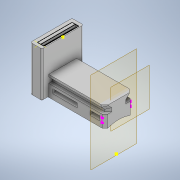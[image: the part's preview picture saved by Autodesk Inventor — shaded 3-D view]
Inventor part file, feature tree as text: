
AUTODESK INVENTOR PART (.ipt)
format: ipt  version: 2021.1 (Build 251245010, 245A)  size: 247,296 bytes
history: native  units: mm
features: move_body x5, extrude x4, sketch x4, direct_edit x2, plane x2, other x1
ambient origin geometry x8: Origin, YZ Plane, XZ Plane, XY Plane, X Axis, Y Axis, Z Axis, Center Point
bodies: Volumenkörper1 (feature_tree)
feature tree (18):
  direct_edit  "Direktbearbeitung1"
  extrude  "Extrusion1"  Depth=5.0mm TaperAngle=0.0deg
  plane  "Arbeitsebene4"
  sketch  "Skizze3"  dims[d6=0.0mm d7=0.0mm d8=-5.0mm d9=0.0mm d10=0.0mm d11=-6.75mm]
  plane  "Arbeitsebene3"
  extrude  "Extrusion2"  TaperAngle=0.0deg  [1 undecoded]
  sketch  "Skizze6"  dims[d18=10.0mm d19=0.0mm d20=2.0mm d21=0.0mm d22=1.9mm d23=0.0mm d24=0.0mm]
  extrude  "Extrusion3"  Depth=5.5mm TaperAngle=0.0deg
  extrude  "Extrusion4"  Depth=2.0mm TaperAngle=0.0deg
  direct_edit  "Direktbearbeitung2"
  sketch  "Skizze1"  dims[d0=0.0mm d1=0.0mm d2=15.75mm d3=5.0mm d4=0.0mm d5=0.0mm]
  sketch  "Skizze5"  dims[d12=10.0mm d13=0.0mm d16=5.5mm d17=0.0mm]
  other  "Körper1"
  move_body  "Verschieben1"
  move_body  "Verschieben2"
  move_body  "Verschieben3"
  move_body  "Verschieben4"
  move_body  "Verschieben5"
note: 1 required parameter value undecoded (feature->parameter linkage not recoverable at this tier; creation-order binding heuristic only, values carry confidence <= 0.55)
